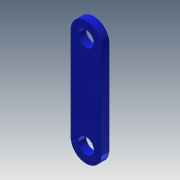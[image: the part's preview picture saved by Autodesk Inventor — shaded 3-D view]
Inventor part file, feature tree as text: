
AUTODESK INVENTOR PART (.ipt)
format: ipt  version: 2013 (Build 170138000, 138)  size: 94,720 bytes
history: native  units: mm
features: sketch x6, extrude x2
ambient origin geometry x8: Origin, YZ Plane, XZ Plane, XY Plane, X Axis, Y Axis, Z Axis, Center Point
bodies: Solid1 (feature_tree)
feature tree (8):
  extrude  "Extrusion1"  Depth=18.0mm
  extrude  "Extrusion2"  Depth=1.5mm TaperAngle=0.0deg
  sketch  "Sketch3"  dims[d5=3.0mm]
  sketch  "Sketch4"  dims[d6=3.0mm]
  sketch  "Sketch5"  dims[d7=2.0mm d8=0.0mm]
  sketch  "Sketch6"
  sketch  "Sketch1"  dims[d0=6.0mm d1=18.0mm]
  sketch  "Sketch2"  dims[d2=6.0mm d3=1.5mm d4=0.0mm]
